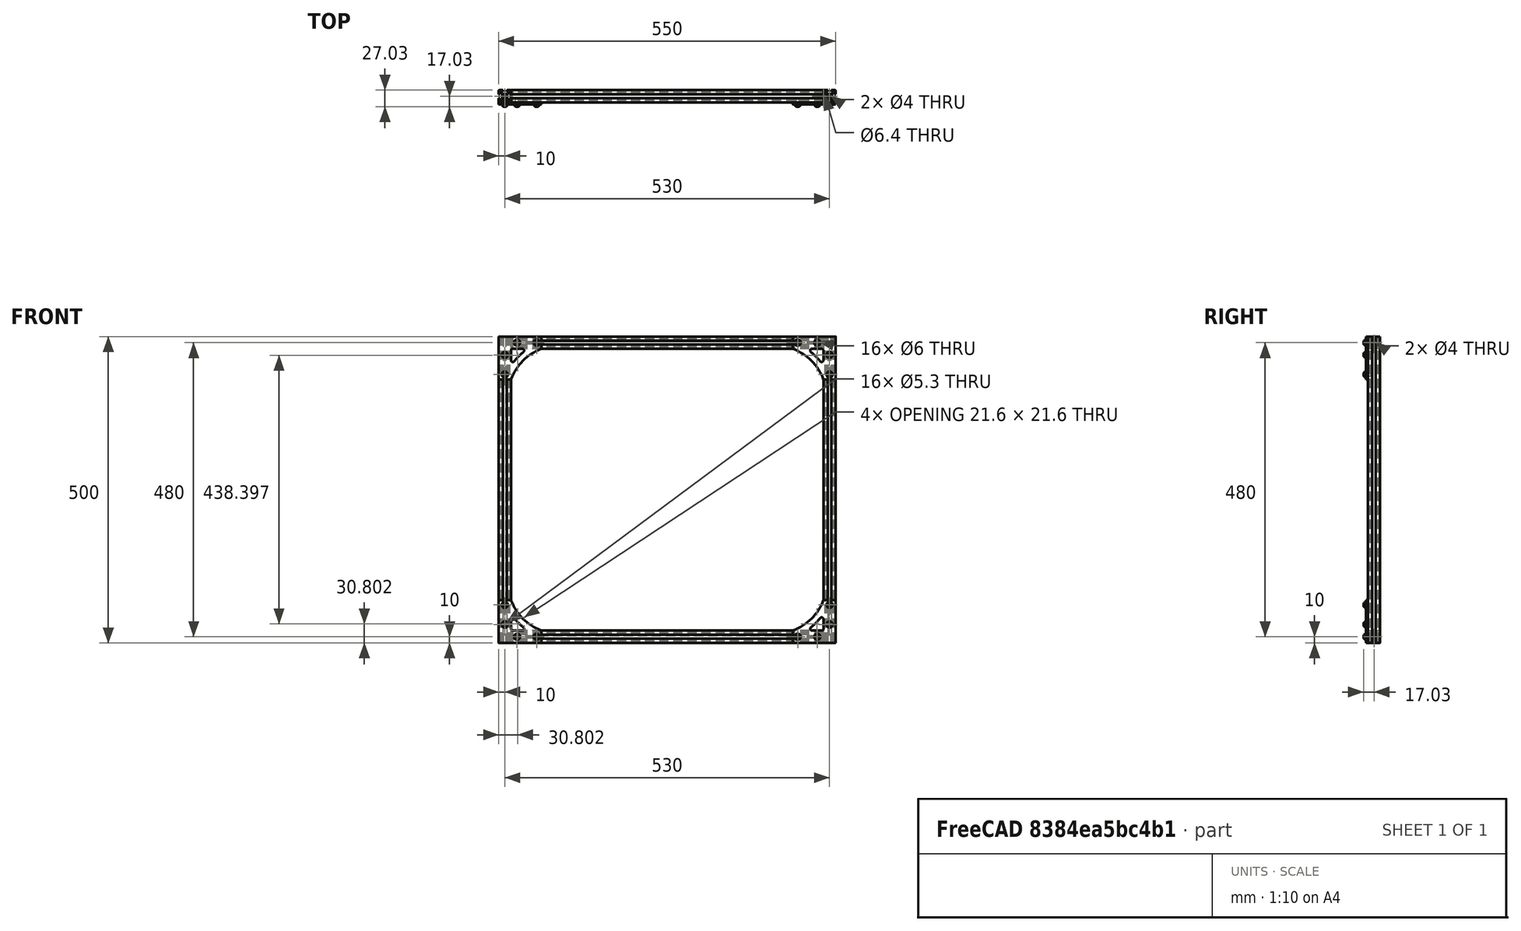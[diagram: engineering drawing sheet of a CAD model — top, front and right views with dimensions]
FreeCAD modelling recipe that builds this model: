
FCSTD DOCUMENT  (FreeCAD 0.17R7796 (Git))
Label: TAZ6_frame_assy
License: CreativeCommons Attribution-ShareAlike
LicenseURL: http://creativecommons.org/licenses/by-sa/4.0/
objects: Part::FeaturePython×42, App::FeaturePython×42
note: 42 computed .brp shape members not serialized (recipe doc carries the construction recipe); baked Part::Feature solids carry a one-line shape summary decoded from their .brp

FEATURE [Part::FeaturePython] _10mm_extrusion_01  # a2plus imported part (geometry in sourceFile) (typed FeaturePython)
  Placement = pos=(0,0,0) rot=(0.57735,0.57735,0.57735;2.0944rad)
  fixedPosition = true
  sourceFile = <userpath>/shared-j/devel/lulzbot/TAZ/Olive/production_parts/jigs/TAZ6_frame_assy_fixture/510mm_extrusion.fcstd
  timeLastImport = 1466531039
  updateColors = true
FEATURE [Part::FeaturePython] _00mm_extrusion_01  # a2plus imported part (geometry in sourceFile) (typed FeaturePython)
  Placement = pos=(10,0,490) rot=(0,0,-1;1.5708rad)
  fixedPosition = false
  sourceFile = <userpath>/shared-j/devel/lulzbot/TAZ/Olive/production_parts/jigs/TAZ6_frame_assy_fixture/500mm_extrusion.fcstd
  timeLastImport = 1466531256
  updateColors = true
FEATURE [App::FeaturePython] planeConstraint01  # a2plus constraint (typed FeaturePython)
  Object1 = _10mm_extrusion_01
  Object2 = _00mm_extrusion_01
  SubElement1 = Face2
  SubElement2 = Face30
  Type = plane
  directionConstraint = 0
  offset = 0
FEATURE [App::FeaturePython] planeConstraint01_mirror  label="planeConstraint01_"  # a2plus constraint (typed FeaturePython)
  Object1 = _10mm_extrusion_01
  Object2 = _00mm_extrusion_01
  SubElement1 = Face2
  SubElement2 = Face30
  Type = plane
  directionConstraint = 0
  offset = 0
FEATURE [App::FeaturePython] planeConstraint02  # a2plus constraint (typed FeaturePython)
  Object1 = _10mm_extrusion_01
  Object2 = _00mm_extrusion_01
  SubElement1 = Face50
  SubElement2 = Face5
  Type = plane
  directionConstraint = 0
  offset = 0
FEATURE [App::FeaturePython] planeConstraint02_mirror  label="planeConstraint02_"  # a2plus constraint (typed FeaturePython)
  Object1 = _10mm_extrusion_01
  Object2 = _00mm_extrusion_01
  SubElement1 = Face50
  SubElement2 = Face5
  Type = plane
  directionConstraint = 0
  offset = 0
FEATURE [App::FeaturePython] planeConstraint03  # a2plus constraint (typed FeaturePython)
  Object1 = _10mm_extrusion_01
  Object2 = _00mm_extrusion_01
  SubElement1 = Face6
  SubElement2 = Face47
  Type = plane
  directionConstraint = 0
  offset = 0
FEATURE [App::FeaturePython] planeConstraint03_mirror  label="planeConstraint03_"  # a2plus constraint (typed FeaturePython)
  Object1 = _10mm_extrusion_01
  Object2 = _00mm_extrusion_01
  SubElement1 = Face6
  SubElement2 = Face47
  Type = plane
  directionConstraint = 0
  offset = 0
FEATURE [Part::FeaturePython] _00mm_extrusion_01001  # a2plus imported part (geometry in sourceFile) (typed FeaturePython)
  Placement = pos=(-520,0,490) rot=(0,0,-1;1.5708rad)
  fixedPosition = false
  sourceFile = <userpath>/shared-j/devel/lulzbot/TAZ/Olive/production_parts/jigs/TAZ6_frame_assy_fixture/500mm_extrusion.fcstd
  timeLastImport = 1466531256
  updateColors = true
FEATURE [App::FeaturePython] planeConstraint04  # a2plus constraint (typed FeaturePython)
  Object1 = _10mm_extrusion_01
  Object2 = _00mm_extrusion_01001
  SubElement1 = Face5
  SubElement2 = Face1
  Type = plane
  directionConstraint = 1
  offset = 0
FEATURE [App::FeaturePython] planeConstraint04_mirror  label="planeConstraint04_"  # a2plus constraint (typed FeaturePython)
  Object1 = _10mm_extrusion_01
  Object2 = _00mm_extrusion_01001
  SubElement1 = Face5
  SubElement2 = Face1
  Type = plane
  directionConstraint = 1
  offset = 0
FEATURE [App::FeaturePython] planeConstraint05  # a2plus constraint (typed FeaturePython)
  Object1 = _00mm_extrusion_01001
  Object2 = _10mm_extrusion_01
  SubElement1 = Face27
  SubElement2 = Face6
  Type = plane
  directionConstraint = 0
  offset = 0
FEATURE [App::FeaturePython] planeConstraint05_mirror  label="planeConstraint05_"  # a2plus constraint (typed FeaturePython)
  Object1 = _00mm_extrusion_01001
  Object2 = _10mm_extrusion_01
  SubElement1 = Face27
  SubElement2 = Face6
  Type = plane
  directionConstraint = 0
  offset = 0
FEATURE [App::FeaturePython] planeConstraint06  # a2plus constraint (typed FeaturePython)
  Object1 = _10mm_extrusion_01
  Object2 = _00mm_extrusion_01001
  SubElement1 = Face30
  SubElement2 = Face5
  Type = plane
  directionConstraint = 0
  offset = 0
FEATURE [App::FeaturePython] planeConstraint06_mirror  label="planeConstraint06_"  # a2plus constraint (typed FeaturePython)
  Object1 = _10mm_extrusion_01
  Object2 = _00mm_extrusion_01001
  SubElement1 = Face30
  SubElement2 = Face5
  Type = plane
  directionConstraint = 0
  offset = 0
FEATURE [Part::FeaturePython] _10mm_extrusion_01001  # a2plus imported part (geometry in sourceFile) (typed FeaturePython)
  Placement = pos=(0,0,480) rot=(0.57735,0.57735,0.57735;2.0944rad)
  fixedPosition = false
  sourceFile = <userpath>/shared-j/devel/lulzbot/TAZ/Olive/production_parts/jigs/TAZ6_frame_assy_fixture/510mm_extrusion.fcstd
  timeLastImport = 1466531039
  updateColors = true
FEATURE [App::FeaturePython] planeConstraint07  # a2plus constraint (typed FeaturePython)
  Object1 = _00mm_extrusion_01
  Object2 = _10mm_extrusion_01001
  SubElement1 = Face47
  SubElement2 = Face26
  Type = plane
  directionConstraint = 0
  offset = 0
FEATURE [App::FeaturePython] planeConstraint07_mirror  label="planeConstraint07_"  # a2plus constraint (typed FeaturePython)
  Object1 = _00mm_extrusion_01
  Object2 = _10mm_extrusion_01001
  SubElement1 = Face47
  SubElement2 = Face26
  Type = plane
  directionConstraint = 0
  offset = 0
FEATURE [App::FeaturePython] planeConstraint08  # a2plus constraint (typed FeaturePython)
  Object1 = _00mm_extrusion_01
  Object2 = _10mm_extrusion_01001
  SubElement1 = Face2
  SubElement2 = Face23
  Type = plane
  directionConstraint = 1
  offset = 0
FEATURE [App::FeaturePython] planeConstraint08_mirror  label="planeConstraint08_"  # a2plus constraint (typed FeaturePython)
  Object1 = _00mm_extrusion_01
  Object2 = _10mm_extrusion_01001
  SubElement1 = Face2
  SubElement2 = Face23
  Type = plane
  directionConstraint = 1
  offset = 0
FEATURE [App::FeaturePython] planeConstraint09  # a2plus constraint (typed FeaturePython)
  Object1 = _00mm_extrusion_01001
  Object2 = _10mm_extrusion_01001
  SubElement1 = Face1
  SubElement2 = Face5
  Type = plane
  directionConstraint = 0
  offset = 0
FEATURE [App::FeaturePython] planeConstraint09_mirror  label="planeConstraint09_"  # a2plus constraint (typed FeaturePython)
  Object1 = _00mm_extrusion_01001
  Object2 = _10mm_extrusion_01001
  SubElement1 = Face1
  SubElement2 = Face5
  Type = plane
  directionConstraint = 0
  offset = 0
FEATURE [Part::FeaturePython] corner_bracket_v2_0_1_01  # a2plus imported part (geometry in sourceFile) (typed FeaturePython)
  Placement = pos=(-530,-10,420) rot=(1,0,0;1.5708rad)
  fixedPosition = false
  sourceFile = <userpath>/shared-j/devel/lulzbot/TAZ/Olive/production_parts/machined_parts/corner_bracket_v2.0/corner_bracket_v2.0.1.FCStd
  timeLastImport = 1442850461
  updateColors = true
FEATURE [App::FeaturePython] planeConstraint10  # a2plus constraint (typed FeaturePython)
  Object1 = _10mm_extrusion_01001
  Object2 = corner_bracket_v2_0_1_01
  SubElement1 = Face1
  SubElement2 = Face6
  Type = plane
  directionConstraint = 0
  offset = 0
FEATURE [App::FeaturePython] planeConstraint10_mirror  label="planeConstraint10_"  # a2plus constraint (typed FeaturePython)
  Object1 = _10mm_extrusion_01001
  Object2 = corner_bracket_v2_0_1_01
  SubElement1 = Face1
  SubElement2 = Face6
  Type = plane
  directionConstraint = 0
  offset = 0
FEATURE [App::FeaturePython] planeConstraint11  # a2plus constraint (typed FeaturePython)
  Object1 = _10mm_extrusion_01001
  Object2 = corner_bracket_v2_0_1_01
  SubElement1 = Face26
  SubElement2 = Face1
  Type = plane
  directionConstraint = 0
  offset = 0
FEATURE [App::FeaturePython] planeConstraint11_mirror  label="planeConstraint11_"  # a2plus constraint (typed FeaturePython)
  Object1 = _10mm_extrusion_01001
  Object2 = corner_bracket_v2_0_1_01
  SubElement1 = Face26
  SubElement2 = Face1
  Type = plane
  directionConstraint = 0
  offset = 0
FEATURE [App::FeaturePython] planeConstraint12  # a2plus constraint (typed FeaturePython)
  Object1 = _00mm_extrusion_01001
  Object2 = corner_bracket_v2_0_1_01
  SubElement1 = Face50
  SubElement2 = Face10
  Type = plane
  directionConstraint = 0
  offset = 0
FEATURE [App::FeaturePython] planeConstraint12_mirror  label="planeConstraint12_"  # a2plus constraint (typed FeaturePython)
  Object1 = _00mm_extrusion_01001
  Object2 = corner_bracket_v2_0_1_01
  SubElement1 = Face50
  SubElement2 = Face10
  Type = plane
  directionConstraint = 0
  offset = 0
FEATURE [Part::FeaturePython] corner_bracket_v2_0_1_01001  # a2plus imported part (geometry in sourceFile) (typed FeaturePython)
  Placement = pos=(-50,-10,490) rot=(0.57735,0.57735,-0.57735;2.0944rad)
  fixedPosition = false
  sourceFile = <userpath>/shared-j/devel/lulzbot/TAZ/Olive/production_parts/machined_parts/corner_bracket_v2.0/corner_bracket_v2.0.1.FCStd
  timeLastImport = 1442850461
  updateColors = true
FEATURE [App::FeaturePython] planeConstraint13  # a2plus constraint (typed FeaturePython)
  Object1 = _10mm_extrusion_01001
  Object2 = corner_bracket_v2_0_1_01001
  SubElement1 = Face1
  SubElement2 = Face10
  Type = plane
  directionConstraint = 0
  offset = 0
FEATURE [App::FeaturePython] planeConstraint13_mirror  label="planeConstraint13_"  # a2plus constraint (typed FeaturePython)
  Object1 = _10mm_extrusion_01001
  Object2 = corner_bracket_v2_0_1_01001
  SubElement1 = Face1
  SubElement2 = Face10
  Type = plane
  directionConstraint = 0
  offset = 0
FEATURE [App::FeaturePython] planeConstraint14  # a2plus constraint (typed FeaturePython)
  Object1 = _10mm_extrusion_01001
  Object2 = corner_bracket_v2_0_1_01001
  SubElement1 = Face6
  SubElement2 = Face1
  Type = plane
  directionConstraint = 0
  offset = 0
FEATURE [App::FeaturePython] planeConstraint14_mirror  label="planeConstraint14_"  # a2plus constraint (typed FeaturePython)
  Object1 = _10mm_extrusion_01001
  Object2 = corner_bracket_v2_0_1_01001
  SubElement1 = Face6
  SubElement2 = Face1
  Type = plane
  directionConstraint = 0
  offset = 0
FEATURE [App::FeaturePython] planeConstraint15  # a2plus constraint (typed FeaturePython)
  Object1 = _00mm_extrusion_01
  Object2 = corner_bracket_v2_0_1_01001
  SubElement1 = Face23
  SubElement2 = Face6
  Type = plane
  directionConstraint = 0
  offset = 0
FEATURE [App::FeaturePython] planeConstraint15_mirror  label="planeConstraint15_"  # a2plus constraint (typed FeaturePython)
  Object1 = _00mm_extrusion_01
  Object2 = corner_bracket_v2_0_1_01001
  SubElement1 = Face23
  SubElement2 = Face6
  Type = plane
  directionConstraint = 0
  offset = 0
FEATURE [Part::FeaturePython] corner_bracket_v2_0_1_01002  # a2plus imported part (geometry in sourceFile) (typed FeaturePython)
  Placement = pos=(20,-10,60) rot=(0,-0.707107,0.707107;3.14159rad)
  fixedPosition = false
  sourceFile = <userpath>/shared-j/devel/lulzbot/TAZ/Olive/production_parts/machined_parts/corner_bracket_v2.0/corner_bracket_v2.0.1.FCStd
  timeLastImport = 1442850461
  updateColors = true
FEATURE [App::FeaturePython] planeConstraint16  # a2plus constraint (typed FeaturePython)
  Object1 = _00mm_extrusion_01
  Object2 = corner_bracket_v2_0_1_01002
  SubElement1 = Face27
  SubElement2 = Face1
  Type = plane
  directionConstraint = 0
  offset = 0
FEATURE [App::FeaturePython] planeConstraint16_mirror  label="planeConstraint16_"  # a2plus constraint (typed FeaturePython)
  Object1 = _00mm_extrusion_01
  Object2 = corner_bracket_v2_0_1_01002
  SubElement1 = Face27
  SubElement2 = Face1
  Type = plane
  directionConstraint = 0
  offset = 0
FEATURE [App::FeaturePython] planeConstraint17  # a2plus constraint (typed FeaturePython)
  Object1 = _10mm_extrusion_01
  Object2 = corner_bracket_v2_0_1_01002
  SubElement1 = Face30
  SubElement2 = Face6
  Type = plane
  directionConstraint = 0
  offset = 0
FEATURE [App::FeaturePython] planeConstraint17_mirror  label="planeConstraint17_"  # a2plus constraint (typed FeaturePython)
  Object1 = _10mm_extrusion_01
  Object2 = corner_bracket_v2_0_1_01002
  SubElement1 = Face30
  SubElement2 = Face6
  Type = plane
  directionConstraint = 0
  offset = 0
FEATURE [App::FeaturePython] planeConstraint18  # a2plus constraint (typed FeaturePython)
  Object1 = _00mm_extrusion_01
  Object2 = corner_bracket_v2_0_1_01002
  SubElement1 = Face23
  SubElement2 = Face10
  Type = plane
  directionConstraint = 0
  offset = 0
FEATURE [App::FeaturePython] planeConstraint18_mirror  label="planeConstraint18_"  # a2plus constraint (typed FeaturePython)
  Object1 = _00mm_extrusion_01
  Object2 = corner_bracket_v2_0_1_01002
  SubElement1 = Face23
  SubElement2 = Face10
  Type = plane
  directionConstraint = 0
  offset = 0
FEATURE [Part::FeaturePython] corner_bracket_v2_0_1_01003  # a2plus imported part (geometry in sourceFile) (typed FeaturePython)
  Placement = pos=(-460,-10,-10) rot=(0.57735,-0.57735,0.57735;2.0944rad)
  fixedPosition = false
  sourceFile = <userpath>/shared-j/devel/lulzbot/TAZ/Olive/production_parts/machined_parts/corner_bracket_v2.0/corner_bracket_v2.0.1.FCStd
  timeLastImport = 1442850461
  updateColors = true
FEATURE [App::FeaturePython] planeConstraint19  # a2plus constraint (typed FeaturePython)
  Object1 = _10mm_extrusion_01
  Object2 = corner_bracket_v2_0_1_01003
  SubElement1 = Face26
  SubElement2 = Face1
  Type = plane
  directionConstraint = 0
  offset = 0
FEATURE [App::FeaturePython] planeConstraint19_mirror  label="planeConstraint19_"  # a2plus constraint (typed FeaturePython)
  Object1 = _10mm_extrusion_01
  Object2 = corner_bracket_v2_0_1_01003
  SubElement1 = Face26
  SubElement2 = Face1
  Type = plane
  directionConstraint = 0
  offset = 0
FEATURE [App::FeaturePython] planeConstraint20  # a2plus constraint (typed FeaturePython)
  Object1 = _10mm_extrusion_01
  Object2 = corner_bracket_v2_0_1_01003
  SubElement1 = Face30
  SubElement2 = Face10
  Type = plane
  directionConstraint = 0
  offset = 0
FEATURE [App::FeaturePython] planeConstraint20_mirror  label="planeConstraint20_"  # a2plus constraint (typed FeaturePython)
  Object1 = _10mm_extrusion_01
  Object2 = corner_bracket_v2_0_1_01003
  SubElement1 = Face30
  SubElement2 = Face10
  Type = plane
  directionConstraint = 0
  offset = 0
FEATURE [App::FeaturePython] planeConstraint21  # a2plus constraint (typed FeaturePython)
  Object1 = _00mm_extrusion_01001
  Object2 = corner_bracket_v2_0_1_01003
  SubElement1 = Face50
  SubElement2 = Face6
  Type = plane
  directionConstraint = 0
  offset = 0
FEATURE [App::FeaturePython] planeConstraint21_mirror  label="planeConstraint21_"  # a2plus constraint (typed FeaturePython)
  Object1 = _00mm_extrusion_01001
  Object2 = corner_bracket_v2_0_1_01003
  SubElement1 = Face50
  SubElement2 = Face6
  Type = plane
  directionConstraint = 0
  offset = 0
FEATURE [Part::FeaturePython] Washer  label="M6-Washer"  # Fasteners workbench fastener (typed FeaturePython)
  diameter = 2
  invert = false
  matchOuter = false
  offset = 0
  type = 1
FEATURE [Part::FeaturePython] Washer001  label="M5-Washer"  # Fasteners workbench fastener (typed FeaturePython)
  Placement = pos=(-520,-13.175,428) rot=(1,0,0;1.5708rad)
  baseObject = -> corner_bracket_v2_0_1_01 [Edge58]
  diameter = 1
  invert = false
  matchOuter = false
  offset = 0
  type = 1
FEATURE [Part::FeaturePython] Washer002  label="M5-Washer001"  # Fasteners workbench fastener (typed FeaturePython)
  Placement = pos=(-520,-13.175,460) rot=(1,0,0;1.5708rad)
  baseObject = -> corner_bracket_v2_0_1_01 [Edge60]
  diameter = 1
  invert = false
  matchOuter = false
  offset = 0
  type = 1
FEATURE [Part::FeaturePython] Washer003  label="M5-Washer002"  # Fasteners workbench fastener (typed FeaturePython)
  Placement = pos=(-500,-13.175,480) rot=(1,0,0;1.5708rad)
  baseObject = -> corner_bracket_v2_0_1_01 [Edge56]
  diameter = 1
  invert = false
  matchOuter = false
  offset = 0
  type = 1
FEATURE [Part::FeaturePython] Washer004  label="M5-Washer003"  # Fasteners workbench fastener (typed FeaturePython)
  Placement = pos=(-468,-13.175,480) rot=(1,0,0;1.5708rad)
  baseObject = -> corner_bracket_v2_0_1_01 [Edge54]
  diameter = 1
  invert = false
  matchOuter = false
  offset = 0
  type = 1
FEATURE [Part::FeaturePython] Screw  label="M5x10-Screw"  # Fasteners workbench fastener (typed FeaturePython)
  Placement = pos=(-520,-14.275,428) rot=(1,0,0;1.5708rad)
  baseObject = -> Washer001 [Edge1]
  diameter = 3
  invert = false
  length = 1
  matchOuter = false
  offset = 0
  thread = false
  type = 20
FEATURE [Part::FeaturePython] Screw001  label="M5x10-Screw001"  # Fasteners workbench fastener (typed FeaturePython)
  Placement = pos=(-520,-14.275,460) rot=(1,0,0;1.5708rad)
  baseObject = -> Washer002 [Edge1]
  diameter = 3
  invert = false
  length = 1
  matchOuter = false
  offset = 0
  thread = false
  type = 20
FEATURE [Part::FeaturePython] Screw002  label="M5x10-Screw002"  # Fasteners workbench fastener (typed FeaturePython)
  Placement = pos=(-500,-14.275,480) rot=(1,0,0;1.5708rad)
  baseObject = -> Washer003 [Edge1]
  diameter = 3
  invert = false
  length = 1
  matchOuter = false
  offset = 0
  thread = false
  type = 20
FEATURE [Part::FeaturePython] Screw003  label="M5x10-Screw003"  # Fasteners workbench fastener (typed FeaturePython)
  Placement = pos=(-468,-14.275,480) rot=(1,0,0;1.5708rad)
  baseObject = -> Washer004 [Edge1]
  diameter = 3
  invert = false
  length = 1
  matchOuter = false
  offset = 0
  thread = false
  type = 20
FEATURE [Part::FeaturePython] Washer005  label="M5-Washer004"  # Fasteners workbench fastener (typed FeaturePython)
  Placement = pos=(-42,-13.175,480) rot=(1,0,0;1.5708rad)
  baseObject = -> corner_bracket_v2_0_1_01001 [Edge58]
  diameter = 1
  invert = false
  matchOuter = false
  offset = 0
  type = 1
FEATURE [Part::FeaturePython] Washer006  label="M5-Washer005"  # Fasteners workbench fastener (typed FeaturePython)
  Placement = pos=(-10,-13.175,480) rot=(1,0,0;1.5708rad)
  baseObject = -> corner_bracket_v2_0_1_01001 [Edge60]
  diameter = 1
  invert = false
  matchOuter = false
  offset = 0
  type = 1
FEATURE [Part::FeaturePython] Washer007  label="M5-Washer006"  # Fasteners workbench fastener (typed FeaturePython)
  Placement = pos=(10,-13.175,460) rot=(1,0,0;1.5708rad)
  baseObject = -> corner_bracket_v2_0_1_01001 [Edge56]
  diameter = 1
  invert = false
  matchOuter = false
  offset = 0
  type = 1
FEATURE [Part::FeaturePython] Washer008  label="M5-Washer007"  # Fasteners workbench fastener (typed FeaturePython)
  Placement = pos=(10,-13.175,428) rot=(1,0,0;1.5708rad)
  baseObject = -> corner_bracket_v2_0_1_01001 [Edge54]
  diameter = 1
  invert = false
  matchOuter = false
  offset = 0
  type = 1
FEATURE [Part::FeaturePython] Screw004  label="M5x10-Screw004"  # Fasteners workbench fastener (typed FeaturePython)
  Placement = pos=(-42,-14.275,480) rot=(1,0,0;1.5708rad)
  baseObject = -> Washer005 [Edge1]
  diameter = 3
  invert = false
  length = 1
  matchOuter = false
  offset = 0
  thread = false
  type = 20
FEATURE [Part::FeaturePython] Screw005  label="M5x10-Screw005"  # Fasteners workbench fastener (typed FeaturePython)
  Placement = pos=(-10,-14.275,480) rot=(1,0,0;1.5708rad)
  baseObject = -> Washer006 [Edge1]
  diameter = 3
  invert = false
  length = 1
  matchOuter = false
  offset = 0
  thread = false
  type = 20
FEATURE [Part::FeaturePython] Screw006  label="M5x10-Screw006"  # Fasteners workbench fastener (typed FeaturePython)
  Placement = pos=(10,-14.275,460) rot=(1,0,0;1.5708rad)
  baseObject = -> Washer007 [Edge1]
  diameter = 3
  invert = false
  length = 1
  matchOuter = false
  offset = 0
  thread = false
  type = 20
FEATURE [Part::FeaturePython] Screw007  label="M5x10-Screw007"  # Fasteners workbench fastener (typed FeaturePython)
  Placement = pos=(10,-14.275,428) rot=(1,0,0;1.5708rad)
  baseObject = -> Washer008 [Edge1]
  diameter = 3
  invert = false
  length = 1
  matchOuter = false
  offset = 0
  thread = false
  type = 20
FEATURE [Part::FeaturePython] Washer009  label="M5-Washer011"  # Fasteners workbench fastener (typed FeaturePython)
  Placement = pos=(10,-13.175,52) rot=(1,0,0;1.5708rad)
  baseObject = -> corner_bracket_v2_0_1_01002 [Edge58]
  diameter = 1
  invert = false
  matchOuter = false
  offset = 0
  type = 1
FEATURE [Part::FeaturePython] Washer010  label="M5-Washer010"  # Fasteners workbench fastener (typed FeaturePython)
  Placement = pos=(10,-13.175,20) rot=(1,0,0;1.5708rad)
  baseObject = -> corner_bracket_v2_0_1_01002 [Edge60]
  diameter = 1
  invert = false
  matchOuter = false
  offset = 0
  type = 1
FEATURE [Part::FeaturePython] Washer011  label="M5-Washer009"  # Fasteners workbench fastener (typed FeaturePython)
  Placement = pos=(-10,-13.175,0) rot=(1,0,0;1.5708rad)
  baseObject = -> corner_bracket_v2_0_1_01002 [Edge56]
  diameter = 1
  invert = false
  matchOuter = false
  offset = 0
  type = 1
FEATURE [Part::FeaturePython] Washer012  label="M5-Washer008"  # Fasteners workbench fastener (typed FeaturePython)
  Placement = pos=(-42,-13.175,0) rot=(1,0,0;1.5708rad)
  baseObject = -> corner_bracket_v2_0_1_01002 [Edge54]
  diameter = 1
  invert = false
  matchOuter = false
  offset = 0
  type = 1
FEATURE [Part::FeaturePython] Screw008  label="M5x10-Screw011"  # Fasteners workbench fastener (typed FeaturePython)
  Placement = pos=(10,-14.275,52) rot=(1,0,0;1.5708rad)
  baseObject = -> Washer009 [Edge1]
  diameter = 3
  invert = false
  length = 1
  matchOuter = false
  offset = 0
  thread = false
  type = 20
FEATURE [Part::FeaturePython] Screw009  label="M5x10-Screw010"  # Fasteners workbench fastener (typed FeaturePython)
  Placement = pos=(10,-14.275,20) rot=(1,0,0;1.5708rad)
  baseObject = -> Washer010 [Edge1]
  diameter = 3
  invert = false
  length = 1
  matchOuter = false
  offset = 0
  thread = false
  type = 20
FEATURE [Part::FeaturePython] Screw010  label="M5x10-Screw009"  # Fasteners workbench fastener (typed FeaturePython)
  Placement = pos=(-10,-14.275,0) rot=(1,0,0;1.5708rad)
  baseObject = -> Washer011 [Edge1]
  diameter = 3
  invert = false
  length = 1
  matchOuter = false
  offset = 0
  thread = false
  type = 20
FEATURE [Part::FeaturePython] Screw011  label="M5x10-Screw008"  # Fasteners workbench fastener (typed FeaturePython)
  Placement = pos=(-42,-14.275,0) rot=(1,0,0;1.5708rad)
  baseObject = -> Washer012 [Edge1]
  diameter = 3
  invert = false
  length = 1
  matchOuter = false
  offset = 0
  thread = false
  type = 20
FEATURE [Part::FeaturePython] Washer013  label="M5-Washer012"  # Fasteners workbench fastener (typed FeaturePython)
  Placement = pos=(-520,-13.175,52) rot=(1,0,0;1.5708rad)
  baseObject = -> corner_bracket_v2_0_1_01003 [Edge54]
  diameter = 1
  invert = false
  matchOuter = false
  offset = 0
  type = 1
FEATURE [Part::FeaturePython] Washer014  label="M5-Washer013"  # Fasteners workbench fastener (typed FeaturePython)
  Placement = pos=(-520,-13.175,20) rot=(1,0,0;1.5708rad)
  baseObject = -> corner_bracket_v2_0_1_01003 [Edge56]
  diameter = 1
  invert = false
  matchOuter = false
  offset = 0
  type = 1
FEATURE [Part::FeaturePython] Washer015  label="M5-Washer014"  # Fasteners workbench fastener (typed FeaturePython)
  Placement = pos=(-500,-13.175,0) rot=(1,0,0;1.5708rad)
  baseObject = -> corner_bracket_v2_0_1_01003 [Edge60]
  diameter = 1
  invert = false
  matchOuter = false
  offset = 0
  type = 1
FEATURE [Part::FeaturePython] Washer016  label="M5-Washer015"  # Fasteners workbench fastener (typed FeaturePython)
  Placement = pos=(-468,-13.175,0) rot=(1,0,0;1.5708rad)
  baseObject = -> corner_bracket_v2_0_1_01003 [Edge58]
  diameter = 1
  invert = false
  matchOuter = false
  offset = 0
  type = 1
FEATURE [Part::FeaturePython] Screw012  label="M5x10-Screw015"  # Fasteners workbench fastener (typed FeaturePython)
  Placement = pos=(-520,-14.275,52) rot=(1,0,0;1.5708rad)
  baseObject = -> Washer013 [Edge1]
  diameter = 3
  invert = false
  length = 1
  matchOuter = false
  offset = 0
  thread = false
  type = 20
FEATURE [Part::FeaturePython] Screw013  label="M5x10-Screw014"  # Fasteners workbench fastener (typed FeaturePython)
  Placement = pos=(-520,-14.275,20) rot=(1,0,0;1.5708rad)
  baseObject = -> Washer014 [Edge1]
  diameter = 3
  invert = false
  length = 1
  matchOuter = false
  offset = 0
  thread = false
  type = 20
FEATURE [Part::FeaturePython] Screw014  label="M5x10-Screw013"  # Fasteners workbench fastener (typed FeaturePython)
  Placement = pos=(-500,-14.275,0) rot=(1,0,0;1.5708rad)
  baseObject = -> Washer015 [Edge1]
  diameter = 3
  invert = false
  length = 1
  matchOuter = false
  offset = 0
  thread = false
  type = 20
FEATURE [Part::FeaturePython] Screw015  label="M5x10-Screw012"  # Fasteners workbench fastener (typed FeaturePython)
  Placement = pos=(-468,-14.275,0) rot=(1,0,0;1.5708rad)
  baseObject = -> Washer016 [Edge1]
  diameter = 3
  invert = false
  length = 1
  matchOuter = false
  offset = 0
  thread = false
  type = 20
FEATURE [Part::FeaturePython] muxedAssembly  # WARN: FeaturePython — macro-defined, semantics opaque (R4)
  type = muxedAssembly
